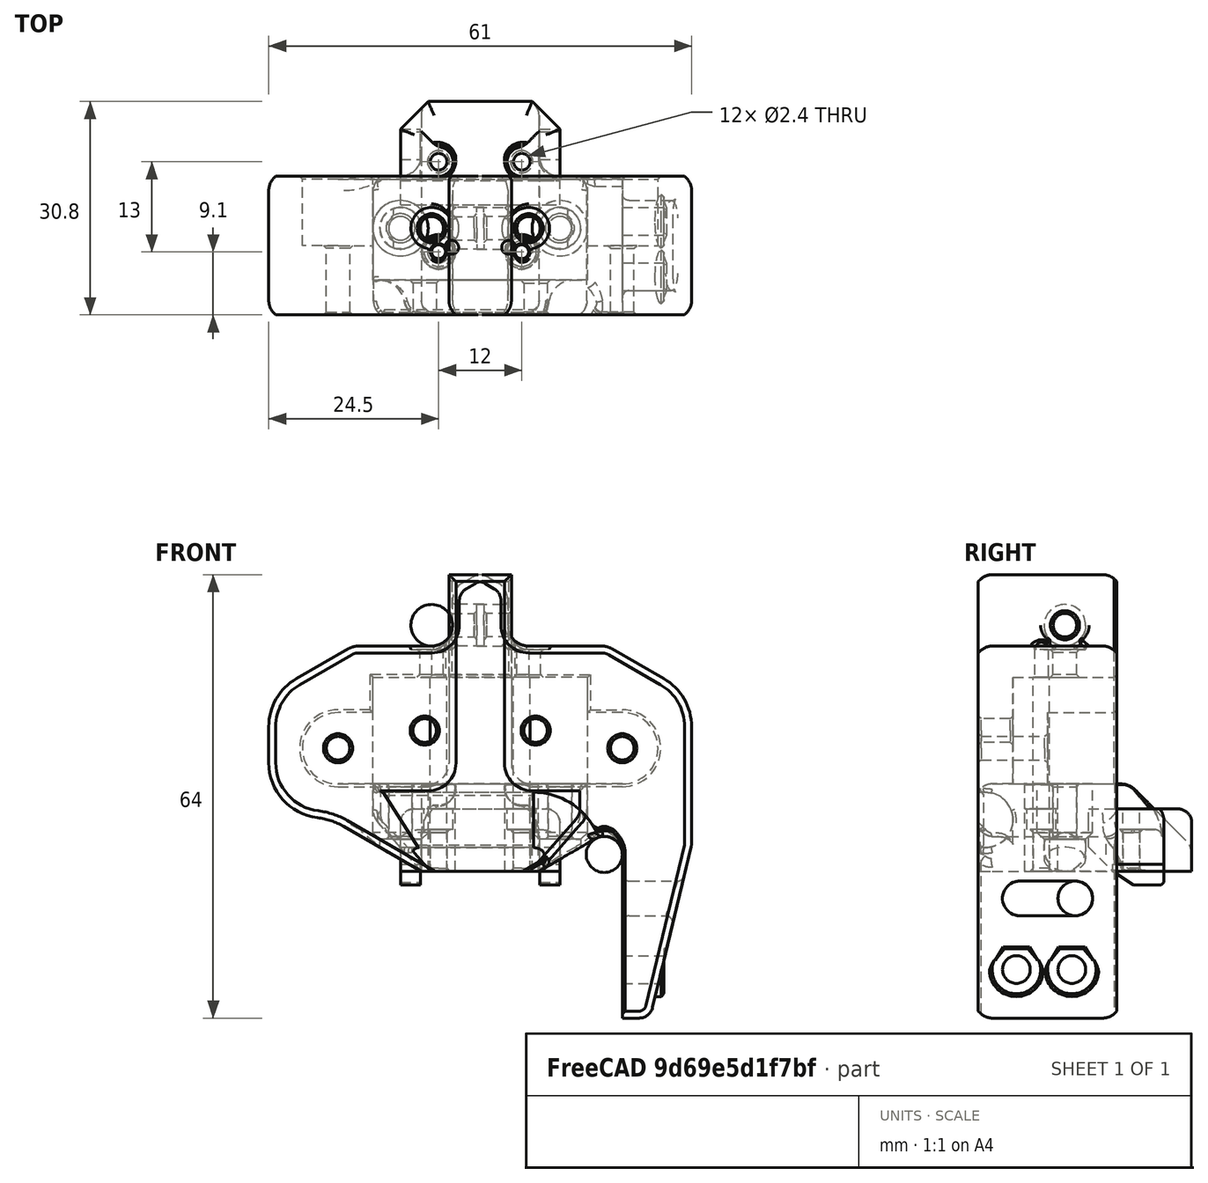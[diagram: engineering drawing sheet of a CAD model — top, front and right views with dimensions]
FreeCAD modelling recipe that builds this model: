
FCSTD DOCUMENT  (FreeCAD 0.18R16146 (Git))
Label: bed-mount-rf
License: All rights reserved
LicenseURL: http://en.wikipedia.org/wiki/All_rights_reserved
objects: Part::Cylinder×18, Part::MultiFuse×10, Part::Feature×6, Part::Chamfer×6, Part::Cut×6, Part::Box×3, Part::Fillet×1
note: 50 computed .brp shape members not serialized (recipe doc carries the construction recipe); baked Part::Feature solids carry a one-line shape summary decoded from their .brp

FEATURE [Part::Feature] Part__Feature887  label="rear bed mount"
  Placement = pos=(-8,-15.4,25.3) rot=(0,0.707107,0.707107;3.14159rad)
  shape: bbox 46.57 x 31.27 x 43.44 mm, 207 faces (baked)
FEATURE [Part::Feature] Part__Feature888  label="rear_bed_mountR"
  Placement = pos=(-17,-15.4,25.3) rot=(0,0.707107,0.707107;3.14159rad)
  shape: bbox 46.58 x 32.66 x 64.02 mm, 313 faces (baked)
FEATURE [Part::Cylinder] Cylinder
  Angle = 360
  AttacherType = Attacher::AttachEngine3D
  Height = 6
  Placement = pos=(6,6.7,0) rot=(0,0,1;0rad)
  Radius = 1.2
FEATURE [Part::Cylinder] Cylinder001
  Angle = 360
  AttacherType = Attacher::AttachEngine3D
  Height = 6
  Placement = pos=(-6,6.7,0) rot=(0,0,1;0rad)
  Radius = 1.2
FEATURE [Part::Box] Box  label="Cube"
  AttacherType = Attacher::AttachEngine3D
  Height = 9
  Length = 23
  Placement = pos=(-11.5,0.5,0) rot=(0,0,1;0rad)
  Width = 14.9
FEATURE [Part::MultiFuse] Fusion
  Shapes = -> [Cylinder,Cylinder001]
FEATURE [Part::Box] Box001  label="Cube001"
  AttacherType = Attacher::AttachEngine3D
  Height = 3
  Length = 2.9
  Placement = pos=(8.6,4,-2) rot=(0,0,1;0rad)
  Width = 7.4
FEATURE [Part::Box] Box002  label="Cube002"
  AttacherType = Attacher::AttachEngine3D
  Height = 3
  Length = 2.9
  Placement = pos=(-11.5,4,-2) rot=(0,0,1;0rad)
  Width = 7.4
FEATURE [Part::MultiFuse] Fusion001
  Shapes = -> [Box001,Box002]
FEATURE [Part::Chamfer] Chamfer
  Base = -> Fusion001
  Edges = 2 edges: [Edge9 r1=2 r2=3,Edge21 r1=2 r2=3]
FEATURE [Part::Chamfer] Chamfer004  label="align-arm"
  Base = -> Chamfer
  Edges = 2 edges r=0.4: [Edge13,Edge28]
FEATURE [Part::Cylinder] Cylinder002
  Angle = 360
  AttacherType = Attacher::AttachEngine3D
  Height = 6
  Placement = pos=(6,6.7,0) rot=(0,0,1;0rad)
  Radius = 1.2
FEATURE [Part::Cylinder] Cylinder003
  Angle = 360
  AttacherType = Attacher::AttachEngine3D
  Height = 6
  Placement = pos=(-6,6.7,0) rot=(0,0,1;0rad)
  Radius = 1.2
FEATURE [Part::Cylinder] Cylinder004
  Angle = 360
  AttacherType = Attacher::AttachEngine3D
  Height = 12
  Placement = pos=(-6,-6.3,0) rot=(0,0,1;0rad)
  Radius = 1.2
FEATURE [Part::Cylinder] Cylinder005
  Angle = 360
  AttacherType = Attacher::AttachEngine3D
  Height = 12
  Placement = pos=(6,-6.3,0) rot=(0,0,1;0rad)
  Radius = 1.2
FEATURE [Part::Cylinder] Cylinder006
  Angle = 360
  AttacherType = Attacher::AttachEngine3D
  Height = 9
  Placement = pos=(6,-6.3,0) rot=(0,0,1;0rad)
  Radius = 2.4
FEATURE [Part::Cylinder] Cylinder007
  Angle = 360
  AttacherType = Attacher::AttachEngine3D
  Height = 9
  Placement = pos=(-6,-6.3,0) rot=(0,0,1;0rad)
  Radius = 2.4
FEATURE [Part::MultiFuse] Fusion003
  Shapes = -> [Cylinder005,Cylinder004]
FEATURE [Part::MultiFuse] Fusion004
  Shapes = -> [Cylinder007,Cylinder006]
FEATURE [Part::Feature] Fusion004001  label="enlarge"
  Placement = pos=(0,0,9) rot=(0,0,1;0rad)
  shape: bbox 16.8 x 4.8 x 9 mm, 6 faces, 2 solids (baked)
FEATURE [Part::Cut] Cut001
  Base = -> Fusion004
  Tool = -> Fusion003
FEATURE [Part::Cylinder] Cylinder008
  Angle = 360
  AttacherType = Attacher::AttachEngine3D
  Height = 28
  Placement = pos=(6,-6.3,0) rot=(0,0,1;0rad)
  Radius = 1.2
FEATURE [Part::Cylinder] Cylinder009
  Angle = 360
  AttacherType = Attacher::AttachEngine3D
  Height = 28
  Placement = pos=(-6,-6.3,0) rot=(0,0,1;0rad)
  Radius = 1.2
FEATURE [Part::MultiFuse] Fusion004002
  Shapes = -> [Cylinder009,Cylinder008]
FEATURE [Part::Chamfer] Chamfer005
  Base = -> Box
  Edges = 1 edges r=3.5: [Edge9]
FEATURE [Part::Chamfer] Chamfer006
  Base = -> Chamfer005
  Edges = 2 edges r=4: [Edge5,Edge15]
FEATURE [Part::Fillet] Fillet
  Base = -> Chamfer006
  Edges = 5 edges r=2: [Edge1,Edge6,Edge8,Edge9,Edge10]
FEATURE [Part::Cylinder] Cylinder010
  Angle = 360
  AttacherType = Attacher::AttachEngine3D
  Height = 28
  Placement = pos=(-6,6.7,0) rot=(0,0,1;0rad)
  Radius = 1.2
FEATURE [Part::Cylinder] Cylinder011
  Angle = 360
  AttacherType = Attacher::AttachEngine3D
  Height = 28
  Placement = pos=(6,6.7,0) rot=(0,0,1;0rad)
  Radius = 1.2
FEATURE [Part::MultiFuse] Fusion004003
  Placement = pos=(0,0,-2) rot=(0,0,1;0rad)
  Shapes = -> [Cylinder011,Cylinder010]
FEATURE [Part::Feature] Fusion004004  label="enlarge001"
  Placement = pos=(0,13,9) rot=(0,0,1;0rad)
  shape: bbox 16.8 x 4.8 x 9 mm, 6 faces, 2 solids (baked)
FEATURE [Part::MultiFuse] Fusion004005
  Shapes = -> [Fusion004004,Fusion004001]
FEATURE [Part::Feature] Fusion004005001  label="Fusion004006"
  shape: bbox 16.8 x 17.8 x 9 mm, 12 faces, 4 solids (baked)
FEATURE [Part::Cut] Cut002  label="left-mounter"
  Base = -> Part__Feature887
  Tool = -> Fusion004005001
FEATURE [Part::Cut] Cut  label="top-rf"
  Base = -> Fillet
  Tool = -> Fusion004003
FEATURE [Part::Cylinder] Cylinder012
  Angle = 360
  AttacherType = Attacher::AttachEngine3D
  Height = 8
  Placement = pos=(11.5,-2.9,4.6) rot=(0,0,1;0rad)
  Radius = 4
FEATURE [Part::Cylinder] Cylinder013
  Angle = 360
  AttacherType = Attacher::AttachEngine3D
  Height = 8
  Placement = pos=(11.5,-2.9,4.6) rot=(0,0,1;0rad)
  Radius = 1.7
FEATURE [Part::Chamfer] Chamfer007
  Base = -> Cylinder012
  Edges = 1 edges r=1: [Edge3]
FEATURE [Part::Cut] Cut003  label="side-rf-1"
  Base = -> Chamfer007
  Tool = -> Cylinder013
FEATURE [Part::Feature] Cut003001  label="side-rf-2"
  Placement = pos=(-23,0,0) rot=(0,0,1;0rad)
  shape: bbox 8 x 8 x 8 mm, 5 faces (baked)
FEATURE [Part::Cut] Cut003002
  Base = -> Part__Feature888
  Tool = -> Fusion004005
FEATURE [Part::Cylinder] Cylinder014
  Angle = 360
  AttacherType = Attacher::AttachEngine3D
  Height = 6
  Placement = pos=(20.5,-1.9,-14.2) rot=(0,1,0;1.5708rad)
  Radius = 3.9
FEATURE [Part::Cylinder] Cylinder015
  Angle = 360
  AttacherType = Attacher::AttachEngine3D
  Height = 6
  Placement = pos=(20.5,-9.9,-14.2) rot=(0,1,0;1.5708rad)
  Radius = 3.9
FEATURE [Part::Cylinder] Cylinder016
  Angle = 360
  AttacherType = Attacher::AttachEngine3D
  Height = 6
  Placement = pos=(20.5,-9.9,-14.2) rot=(0,1,0;1.5708rad)
  Radius = 2
FEATURE [Part::Cylinder] Cylinder017
  Angle = 360
  AttacherType = Attacher::AttachEngine3D
  Height = 6
  Placement = pos=(20.5,-1.9,-14.2) rot=(0,1,0;1.5708rad)
  Radius = 2
FEATURE [Part::MultiFuse] Fusion004005002
  Shapes = -> [Cylinder017,Cylinder016]
FEATURE [Part::MultiFuse] Fusion004005003
  Shapes = -> [Cylinder015,Cylinder014]
FEATURE [Part::Chamfer] Chamfer008
  Base = -> Fusion004005003
  Edges = 2 edges r=0.4: [Edge1,Edge4]
FEATURE [Part::MultiFuse] Fusion004005004
  Shapes = -> [Chamfer008,Cut003002]
FEATURE [Part::Cut] Cut003003  label="right-mounter"
  Base = -> Fusion004005004
  Tool = -> Fusion004005002
